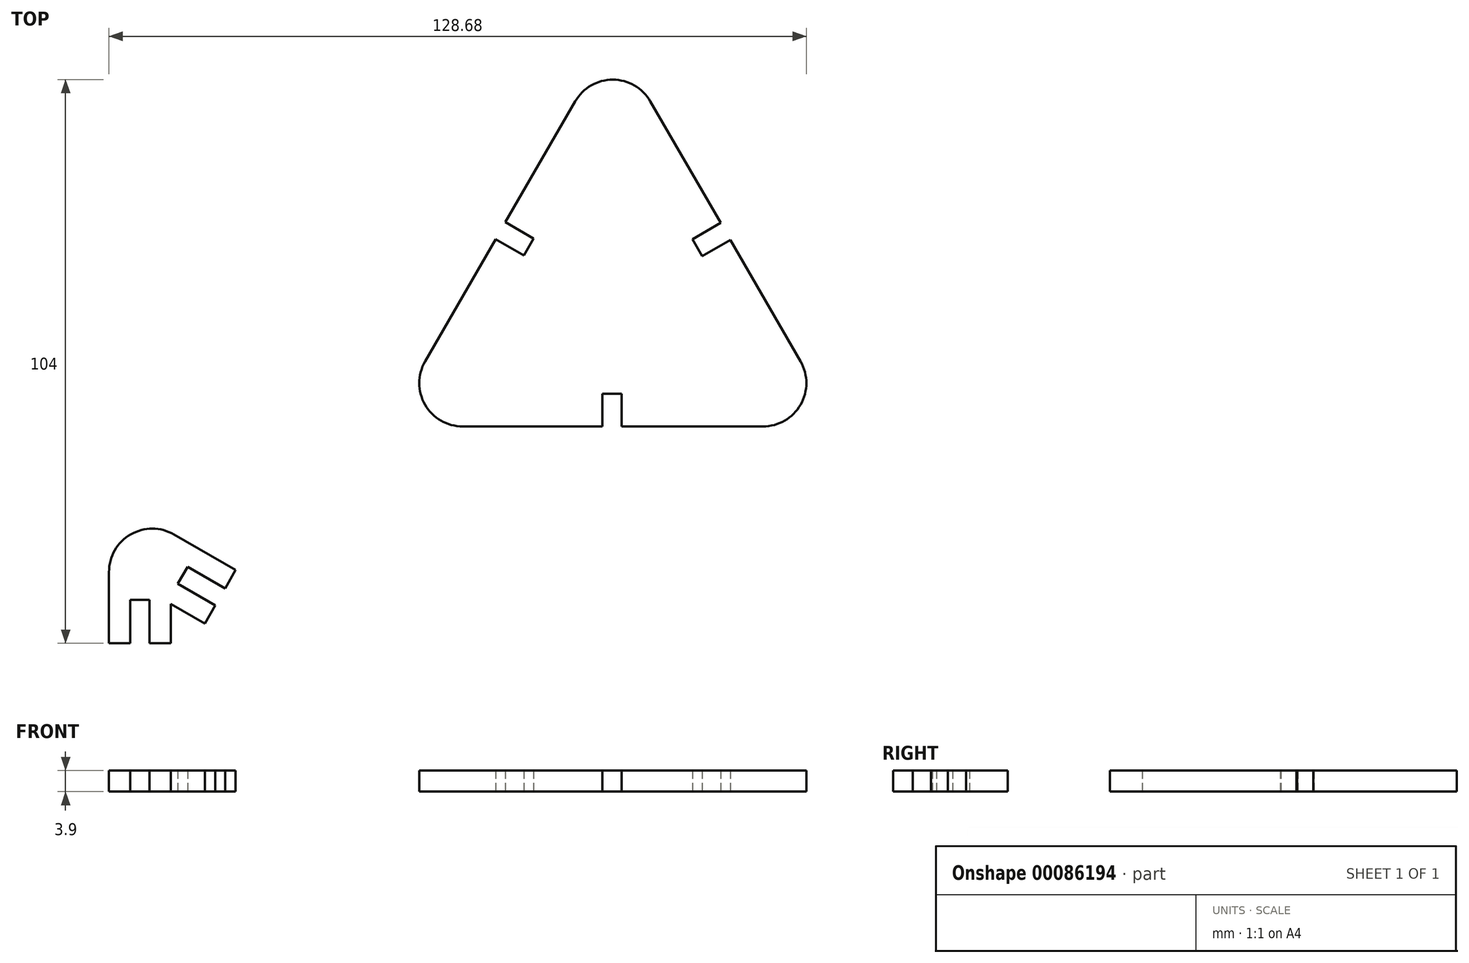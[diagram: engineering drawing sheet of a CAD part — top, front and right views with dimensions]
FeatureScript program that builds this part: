
annotation { "Feature Type Name" : "Feature", "Feature Type Description" : "" }
export const myFeature = defineFeature(function(context is Context, id is Id, definition is map)
    precondition{}
    {
        {
            assignVariable(context, id + "F0", {"name" : "sheet_height", "anyValue" : 3.9});
        }
        {
            var Q0;
            Q0=qCreatedBy(makeId("Top.planeOp"),FACE);
            var sketch = newSketch(context, id + "F1", { "sketchPlane" : qUnion([Q0])});
            skLineSegment(sketch, "E0", {"start": v(13.86, 0) * mm, "end": v(69.28, 0) * mm});
            skLineSegment(sketch, "E1", {"start": v(76.21, 12) * mm, "end": v(48.5, 60) * mm});
            skLineSegment(sketch, "E2", {"start": v(34.64, 60) * mm, "end": v(6.93, 12) * mm});
            skLineSegment(sketch, "E3", {"start": v(41.57, 72) * mm, "end": v(41.57, 0) * mm, "construction": true});
            skLineSegment(sketch, "E4", {"start": v(83.14, 0) * mm, "end": v(20.78, 36) * mm, "construction": true});
            skLineSegment(sketch, "E5", {"start": v(0, 0) * mm, "end": v(62.35, 36) * mm, "construction": true});
            skLineSegment(sketch, "E6", {"start": v(21.76, 37.69) * mm, "end": v(26.96, 34.69) * mm});
            skLineSegment(sketch, "E7", {"start": v(26.96, 34.69) * mm, "end": v(25.16, 31.57) * mm});
            skLineSegment(sketch, "E8", {"start": v(25.16, 31.57) * mm, "end": v(19.96, 34.57) * mm});
            skLineSegment(sketch, "E9", {"start": v(61.45, 37.56) * mm, "end": v(56.26, 34.56) * mm});
            skLineSegment(sketch, "E10", {"start": v(56.26, 34.56) * mm, "end": v(58.06, 31.44) * mm});
            skLineSegment(sketch, "E11", {"start": v(58.06, 31.44) * mm, "end": v(63.25, 34.44) * mm});
            skLineSegment(sketch, "E12", {"start": v(39.62, 0) * mm, "end": v(39.62, 6) * mm});
            skLineSegment(sketch, "E13", {"start": v(39.62, 6) * mm, "end": v(43.22, 6) * mm});
            skLineSegment(sketch, "E14", {"start": v(43.22, 6) * mm, "end": v(43.22, 0) * mm});
            skPoint(sketch, "E15.visualSharp", {"position": v(41.57, 72) * mm});
            skArc(sketch, "E15.filletArc", {"start": v(48.5, 60) * mm, "mid": v(41.57, 64) * mm, "end": v(34.64, 60) * mm});
            skPoint(sketch, "E16.visualSharp", {"position": v(0, 0) * mm});
            skArc(sketch, "E16.filletArc", {"start": v(6.93, 12) * mm, "mid": v(6.93, 4) * mm, "end": v(13.86, 0) * mm});
            skPoint(sketch, "E17.visualSharp", {"position": v(83.14, 0) * mm});
            skArc(sketch, "E17.filletArc", {"start": v(69.28, 0) * mm, "mid": v(76.21, 4) * mm, "end": v(76.21, 12) * mm});
            skSolve(sketch);
        }
        {
            var Q0;
            {var subQ7=sQuery(id+"F1.wireOp",EDGE,"E6");Q0=makeQuery(id+"F1.imprint","IMPRINT",FACE,{"disambiguationData":[TD([[makeQuery(id+"F1.imprint","IMPRINT",EDGE,{"derivedFrom":subQ7}),1.0]])]});}
            extrude(context, id + "F2", {"entities" : qUnion([Q0]), "depth" : (getVariable(context, 'sheet_height')) * mm});
        }
        {
            var Q0;
            Q0=qCreatedBy(makeId("Top.planeOp"),FACE);
            var sketch = newSketch(context, id + "F3", { "sketchPlane" : qUnion([Q0])});
            skLineSegment(sketch, "E18", {"start": v(0, 0) * mm, "end": v(0, -40) * mm, "construction": true});
            skLineSegment(sketch, "E19", {"start": v(0, -40) * mm, "end": v(82.54, -40) * mm});
            skLineSegment(sketch, "E20", {"start": v(82.54, -40) * mm, "end": v(41.27, 16.8) * mm});
            skLineSegment(sketch, "E21", {"start": v(41.27, 16.8) * mm, "end": v(0, -40) * mm});
            skLineSegment(sketch, "E22", {"start": v(41.27, 16.8) * mm, "end": v(41.27, -40) * mm, "construction": true});
            skLineSegment(sketch, "E23", {"start": v(0, -40) * mm, "end": v(54.02, -0.75) * mm, "construction": true});
            skLineSegment(sketch, "E24", {"start": v(82.54, -40) * mm, "end": v(28.52, -0.75) * mm, "construction": true});
            skLineSegment(sketch, "E25", {"start": v(19.49, -13.18) * mm, "end": v(24.34, -16.7) * mm});
            skLineSegment(sketch, "E26", {"start": v(24.34, -16.7) * mm, "end": v(26.46, -13.8) * mm});
            skLineSegment(sketch, "E27", {"start": v(26.46, -13.8) * mm, "end": v(21.6, -10.27) * mm});
            skLineSegment(sketch, "E28", {"start": v(60.93, -10.27) * mm, "end": v(56.08, -13.8) * mm});
            skLineSegment(sketch, "E29", {"start": v(56.08, -13.8) * mm, "end": v(58.2, -16.7) * mm});
            skLineSegment(sketch, "E30", {"start": v(58.2, -16.7) * mm, "end": v(63.05, -13.18) * mm});
            skLineSegment(sketch, "E31", {"start": v(39.62, -40) * mm, "end": v(39.62, -34) * mm});
            skLineSegment(sketch, "E32", {"start": v(39.62, -34) * mm, "end": v(43.22, -34) * mm});
            skLineSegment(sketch, "E33", {"start": v(43.22, -34) * mm, "end": v(43.22, -40) * mm});
            skPoint(sketch, "E34", {"position": v(20.63, -11.6) * mm});
            skPoint(sketch, "E35", {"position": v(61.9, -11.6) * mm});
            skSolve(sketch);
        }
        {
            var Q0;
            Q0=qCreatedBy(makeId("Top.planeOp"),FACE);
            var sketch = newSketch(context, id + "F4", { "sketchPlane" : qUnion([Q0])});
            skLineSegment(sketch, "E36", {"start": v(0, -40) * mm, "end": v(-40, -40) * mm, "construction": true});
            skLineSegment(sketch, "E37", {"start": v(-40, -40) * mm, "end": v(-40, -32.75) * mm});
            skLineSegment(sketch, "E38", {"start": v(-43.9, -40) * mm, "end": v(-40, -40) * mm});
            skLineSegment(sketch, "E39", {"start": v(-43.9, -40) * mm, "end": v(-43.9, -32) * mm});
            skLineSegment(sketch, "E40", {"start": v(-43.9, -32) * mm, "end": v(-47.5, -32) * mm});
            skLineSegment(sketch, "E41", {"start": v(-47.5, -32) * mm, "end": v(-47.5, -40) * mm});
            skLineSegment(sketch, "E42", {"start": v(-47.5, -40) * mm, "end": v(-51.4, -40) * mm});
            skLineSegment(sketch, "E43", {"start": v(-51.4, -40) * mm, "end": v(-51.4, -26.87) * mm});
            skLineSegment(sketch, "E44", {"start": v(-39.4, -19.94) * mm, "end": v(-28.03, -26.5) * mm});
            skLineSegment(sketch, "E45", {"start": v(-28.03, -26.5) * mm, "end": v(-29.98, -29.88) * mm});
            skLineSegment(sketch, "E46", {"start": v(-29.98, -29.88) * mm, "end": v(-36.9, -25.88) * mm});
            skLineSegment(sketch, "E47", {"start": v(-36.9, -25.88) * mm, "end": v(-38.7, -29) * mm});
            skLineSegment(sketch, "E48", {"start": v(-38.7, -29) * mm, "end": v(-31.78, -33) * mm});
            skLineSegment(sketch, "E49", {"start": v(-31.78, -33) * mm, "end": v(-33.73, -36.38) * mm});
            skLineSegment(sketch, "E50", {"start": v(-33.73, -36.38) * mm, "end": v(-40, -32.75) * mm});
            skLineSegment(sketch, "E51", {"start": v(-51.4, -13) * mm, "end": v(-40, -32.75) * mm, "construction": true});
            skLineSegment(sketch, "E52", {"start": v(-38.7, -29) * mm, "end": v(-43.9, -26) * mm, "construction": true});
            skPoint(sketch, "E53.visualSharp", {"position": v(-51.4, -13) * mm});
            skArc(sketch, "E53.filletArc", {"start": v(-39.4, -19.94) * mm, "mid": v(-47.4, -19.94) * mm, "end": v(-51.4, -26.87) * mm});
            skSolve(sketch);
        }
        {
            var Q0;
            Q0=makeQuery(id+"F4.imprint","IMPRINT",FACE,{"disambiguationData":[TD([[makeQuery(id+"F4.imprint","IMPRINT",EDGE,{"derivedFrom":sQuery(id+"F4.wireOp",EDGE,"E37")}),1.0]])]});
            extrude(context, id + "F5", {"entities" : qUnion([Q0]), "depth" : (getVariable(context, 'sheet_height')) * mm});
        }
    });
